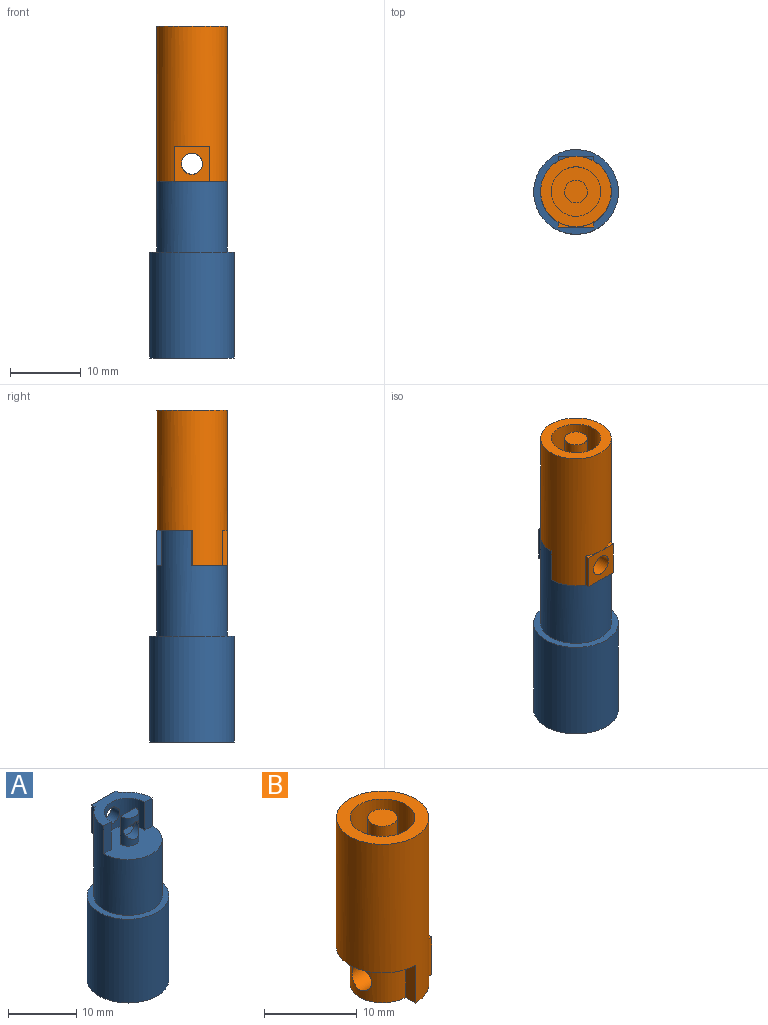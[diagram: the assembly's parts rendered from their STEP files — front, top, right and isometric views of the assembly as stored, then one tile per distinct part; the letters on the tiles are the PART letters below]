
ASSEMBLY  parts=2 mates=1
PART A: 23 faces, bbox 12x12x30 mm
  f0: plane 10x8.5mm, normal (0,0,1), area 54.5mm2, adj f8,f11,f12,f16,f18,f19
  f1: cylinder r=6mm len=15mm, axis (0,0,-1), area 565.5mm2, adj f2,f3
  f2: plane 12x12mm, normal (0,0,1), area 34.6mm2, adj f1,f8
  f3: plane 12x12mm, normal (0,0,-1), area 34.6mm2, adj f1,f5
  f4: cylinder r=3.9mm len=10mm, axis (0,0,-1), area 245mm2, adj f6,f7
  f5: cylinder r=5mm len=10mm, axis (0,0,-1), area 314.2mm2, adj f3,f6
  f6: plane 10x10mm, normal (0,0,-1), area 30.8mm2, adj f4,f5
  f7: plane 7.8x7.8mm, normal (0,0,-1), area 47.8mm2, adj f4
  f8: cylinder r=5mm len=15mm, axis (0,0,-1), area 366.5mm2, adj f0,f2,f9,f10,f12,f13,f15,f16
  f9: plane 2.5x0.67mm, normal (0,0,-1), area 0.5mm2, adj f8,f13,f14
  f10: plane 2.5x0.67mm, normal (0,0,-1), area 0.5mm2, adj f8,f14,f15
  f11: cylinder r=3.5mm len=7mm, axis (0,0,-1), area 47.7mm2, adj f0,f12,f16,f17,f22
  f12: plane 5x1.5mm, normal (0,-1,0), area 7.5mm2, adj f0,f8,f11,f17
  f13: plane 5x0.67mm, normal (1,0,0), area 3.3mm2, adj f8,f9,f14,f17
  f14: plane 5x5mm, normal (0,1,0), area 17.9mm2, adj f9,f10,f13,f15,f17,f22
  f15: plane 5x0.67mm, normal (-1,0,0), area 3.3mm2, adj f8,f10,f14,f17
  f16: plane 5x1.5mm, normal (0,-1,0), area 7.5mm2, adj f0,f8,f11,f17
  f17: plane 10x5mm, normal (0,0,1), area 21.1mm2, adj f8,f11,f12,f13,f14,f15,f16
  f18: plane 5x3.2mm, normal (0,1,0), area 8.9mm2, adj f0,f19,f20,f21
  f19: cylinder r=1.6mm len=5mm, axis (0,0,-1), area 16.7mm2, adj f0,f18,f20,f21
  f20: plane 3.2x1.6mm, normal (0,0,1), area 4mm2, adj f18,f19
  f21: cylinder r=1.5mm len=3mm, axis (0,1,0), area 10.8mm2, adj f18,f19
  f22: cylinder r=1.5mm len=3mm, axis (0,1,0), area 15.7mm2, adj f11,f14
PART B: 21 faces, bbox 10x10x22 mm
  f0: cylinder r=5mm len=22mm, axis (0,0,-1), area 586.4mm2, adj f1,f4,f8,f9,f10,f14,f16,f17
  f1: plane 10x8.5mm, normal (0,0,-1), area 55.6mm2, adj f0,f7,f8,f9,f11,f12,f14,f15
  f2: plane 7x7mm, normal (0,0,1), area 30.4mm2, adj f3,f5
  f3: cylinder r=3.5mm len=7mm, axis (0,0,-1), area 153.9mm2, adj f2,f4
  f4: plane 10x10mm, normal (0,0,1), area 40.1mm2, adj f0,f3
  f5: cylinder r=1.6mm len=7mm, axis (0,0,-1), area 70.4mm2, adj f2,f6
  f6: plane 3.2x3.2mm, normal (0,0,1), area 8mm2, adj f5
  f7: cylinder r=3.5mm len=7mm, axis (0,0,-1), area 47.7mm2, adj f1,f8,f9,f10,f20
  f8: plane 5x1.5mm, normal (-1,0,0), area 7.5mm2, adj f0,f1,f7,f10
  f9: plane 5x1.5mm, normal (-1,0,0), area 7.5mm2, adj f0,f1,f7,f10
  f10: plane 10x5mm, normal (0,0,-1), area 20mm2, adj f0,f7,f8,f9
  f11: cylinder r=1.6mm len=5mm, axis (0,0,-1), area 16.8mm2, adj f1,f12,f13,f19
  f12: plane 5x3.2mm, normal (1,0,0), area 8.9mm2, adj f1,f11,f13,f20
  f13: plane 3.2x1.6mm, normal (0,0,-1), area 4mm2, adj f11,f12
  f14: plane 5x0.67mm, normal (0,-1,0), area 3.3mm2, adj f0,f1,f15,f16
  f15: plane 5x5mm, normal (1,0,0), area 17.9mm2, adj f1,f14,f16,f17,f18,f19
  f16: plane 2.5x0.67mm, normal (0,0,1), area 0.5mm2, adj f0,f14,f15
  f17: plane 5x0.67mm, normal (0,1,0), area 3.3mm2, adj f0,f1,f15,f18
  f18: plane 2.5x0.67mm, normal (0,0,1), area 0.5mm2, adj f0,f15,f17
  f19: cylinder r=1.5mm len=4.44mm, axis (1,0,0), area 36.4mm2, adj f11,f15
  f20: cylinder r=1.5mm len=3.5mm, axis (1,0,0), area 31.4mm2, adj f7,f12
PLACE A t=(-23.19,19.33,-11.33)mm
PLACE B rot(axis=(0,0,-1),90deg) t=(10.8,36.97,13.67)mm
MATE fastened B.f0 <-> A.f1  axis (0,0,-1) through (-10.96,-3.88,13.67)mm
